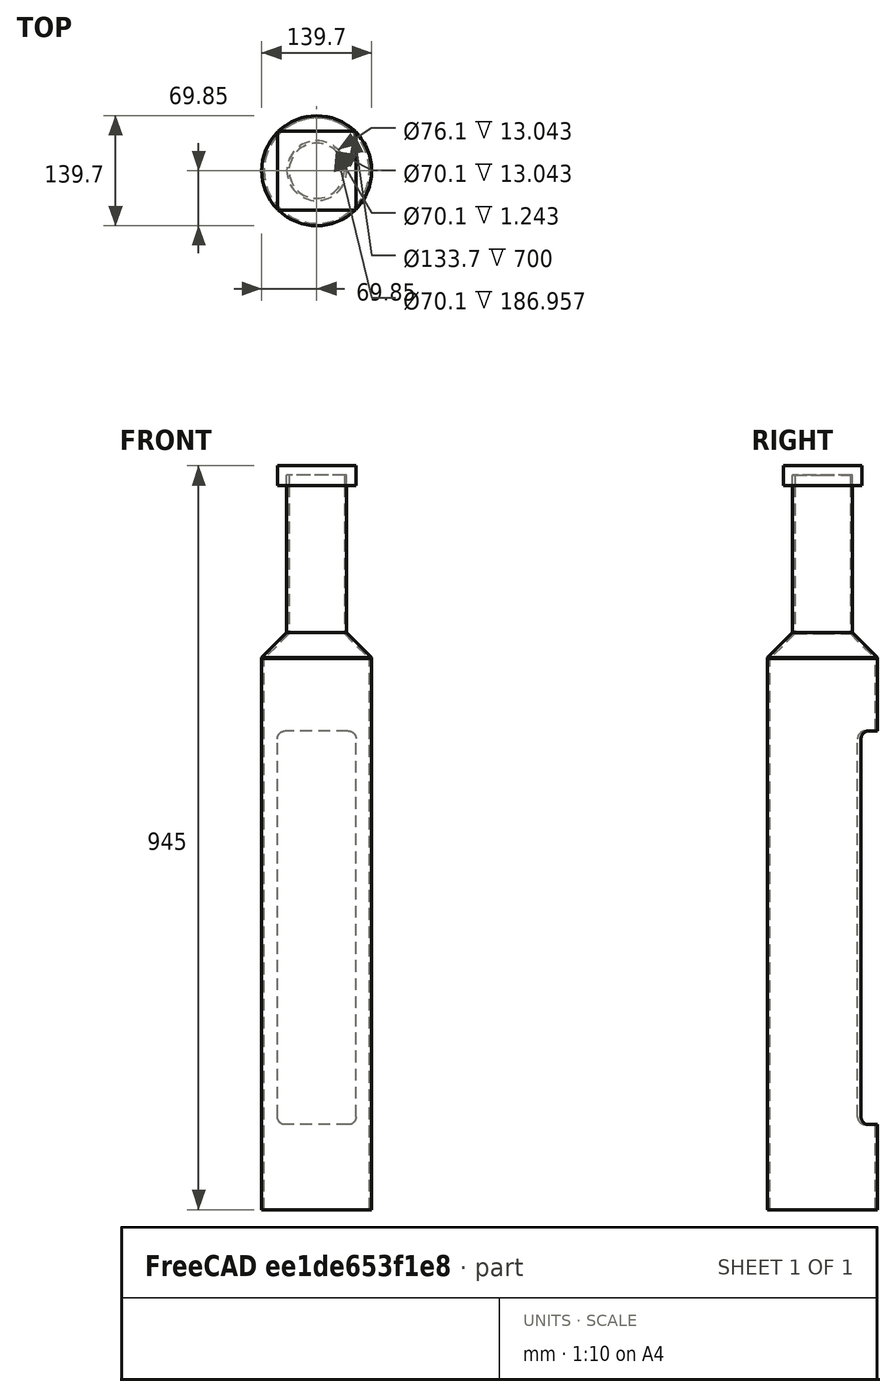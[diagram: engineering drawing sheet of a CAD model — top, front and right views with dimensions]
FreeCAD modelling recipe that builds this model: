
FCSTD DOCUMENT  (FreeCAD 0.21R33694 (Git))
Label: transition2
License: All rights reserved
LicenseURL: http://en.wikipedia.org/wiki/All_rights_reserved
objects: Sketcher::SketchObject×4, Fem::ConstraintForce×4, Part::Revolution×3, Part::FeaturePython×2, Part::Extrusion×1, Part::Cut×1, Part::Box×1, Fem::ConstraintFixed×1, Fem::FemMeshObjectPython×1, App::MaterialObjectPython×1, Fem::FemSolverObjectPython×1, Fem::FemAnalysis×1
note: 12 computed .brp shape members not serialized (recipe doc carries the construction recipe); baked Part::Feature solids carry a one-line shape summary decoded from their .brp

FEATURE [Sketcher::SketchObject] Sketch
  FullyConstrained = true
  Placement = pos=(0,0,0) rot=(1,0,0;1.5708rad)
  sketch-geometry (6):
    g0: LineSegment StartX=66.85 StartY=0 StartZ=0 EndX=69.85 EndY=0 EndZ=0
    g1: LineSegment StartX=35.05 StartY=33.0426 StartZ=0 EndX=38.05 EndY=33.0426 EndZ=0
    g2: LineSegment StartX=35.05 StartY=33.0426 StartZ=0 EndX=35.05 EndY=31.8 EndZ=0
    g3: LineSegment StartX=69.85 StartY=0 StartZ=0 EndX=69.85 EndY=1.24264 EndZ=0
    g4: LineSegment StartX=35.05 StartY=31.8 StartZ=0 EndX=66.85 EndY=0 EndZ=0
    g5: LineSegment StartX=38.05 StartY=33.0426 StartZ=0 EndX=69.85 EndY=1.24264 EndZ=0
  constraints (18):
    c: PointOnObject(g0,g-1)
    c: DistanceX(g-1,g1) = 35.05
    c: DistanceX(g-1,g0) = 66.85
    c: DistanceX(g0,g0) = 3
    c: Horizontal(g0)
    c: Horizontal(g1)
    c: DistanceX(g1,g1) = 3
    c: Coincident(g2,g1)
    c: Vertical(g2)
    c: Coincident(g3,g0)
    c: Vertical(g3)
    c: Coincident(g4,g2)
    c: Coincident(g4,g0)
    c: Coincident(g5,g1)
    c: Coincident(g5,g3)
    c: Angle(g4,g-1) = 0.785398
    c: DistanceY(g2,g2) = 1.24264
    c: DistanceY(g3,g3) = 1.24264
FEATURE [Sketcher::SketchObject] Sketch001
  ExternalGeometry = -> [Sketch]
  FullyConstrained = true
  Placement = pos=(0,0,0) rot=(1,0,0;1.5708rad)
  sketch-geometry (4):
    g0: LineSegment StartX=35.05 StartY=33.0426 StartZ=0 EndX=38.05 EndY=33.0426 EndZ=0
    g1: LineSegment StartX=38.05 StartY=33.0426 StartZ=0 EndX=38.05 EndY=233.043 EndZ=0
    g2: LineSegment StartX=38.05 StartY=233.043 StartZ=0 EndX=35.05 EndY=233.043 EndZ=0
    g3: LineSegment StartX=35.05 StartY=233.043 StartZ=0 EndX=35.05 EndY=33.0426 EndZ=0
  constraints (11):
    c: Coincident(g0,g1)
    c: Coincident(g1,g2)
    c: Coincident(g2,g3)
    c: Coincident(g3,g0)
    c: Horizontal(g0)
    c: Horizontal(g2)
    c: Vertical(g1)
    c: Vertical(g3)
    c: Coincident(g0,g-3)
    c: DistanceY(g1,g1) = 200
    c: DistanceX(g0,g0) = 3
FEATURE [Sketcher::SketchObject] Sketch002
  ExternalGeometry = -> [Sketch]
  FullyConstrained = true
  Placement = pos=(0,0,0) rot=(1,0,0;1.5708rad)
  sketch-geometry (4):
    g0: LineSegment StartX=66.85 StartY=0 StartZ=0 EndX=69.85 EndY=0 EndZ=0
    g1: LineSegment StartX=69.85 StartY=0 StartZ=0 EndX=69.85 EndY=-700 EndZ=0
    g2: LineSegment StartX=69.85 StartY=-700 StartZ=0 EndX=66.85 EndY=-700 EndZ=0
    g3: LineSegment StartX=66.85 StartY=-700 StartZ=0 EndX=66.85 EndY=0 EndZ=0
  constraints (11):
    c: Coincident(g0,g1)
    c: Coincident(g1,g2)
    c: Coincident(g2,g3)
    c: Coincident(g3,g0)
    c: Horizontal(g0)
    c: Horizontal(g2)
    c: Vertical(g1)
    c: Vertical(g3)
    c: Coincident(g0,g-3)
    c: DistanceX(g0,g0) = 3
    c: DistanceY(g1,g1) = 700
FEATURE [Part::Revolution] Revolve
  Angle = 360
  Axis = (0,0,1)
  Base = (0,0,0)
  FaceMakerClass = Part::FaceMakerBullseye
  Solid = true
  Source = -> Sketch
  Symmetric = false
FEATURE [Part::Revolution] Revolve001
  Angle = 360
  Axis = (0,0,1)
  Base = (0,0,0)
  FaceMakerClass = Part::FaceMakerBullseye
  Solid = true
  Source = -> Sketch001
  Symmetric = false
FEATURE [Part::Revolution] Revolve002
  Angle = 360
  Axis = (0,0,1)
  Base = (0,0,0)
  FaceMakerClass = Part::FaceMakerBullseye
  Solid = true
  Source = -> Sketch002
  Symmetric = false
FEATURE [Part::FeaturePython] BooleanFragments  # WARN: FeaturePython — macro-defined, semantics opaque (R4)
  Mode = 2
  Objects = -> [Revolve,Revolve001,Revolve002]
  Tolerance = 0
FEATURE [Sketcher::SketchObject] Sketch003
  ExternalGeometry = -> [Sketch]
  FullyConstrained = true
  Placement = pos=(0,70,0) rot=(0,0.707107,0.707107;3.14159rad)
  sketch-geometry (8):
    g0: LineSegment StartX=-40 StartY=-91.9574 StartZ=0 EndX=40 EndY=-91.9574 EndZ=0
    g1: LineSegment StartX=50 StartY=-101.957 StartZ=0 EndX=50 EndY=-581.957 EndZ=0
    g2: LineSegment StartX=40 StartY=-591.957 StartZ=0 EndX=-40 EndY=-591.957 EndZ=0
    g3: LineSegment StartX=-50 StartY=-581.957 StartZ=0 EndX=-50 EndY=-101.957 EndZ=0
    g4: ArcOfCircle CenterX=-40 CenterY=-101.957 CenterZ=0 NormalX=0 NormalY=0 NormalZ=1 AngleXU=0 Radius=10 StartAngle=1.5708 EndAngle=3.14159
    g5: ArcOfCircle CenterX=40 CenterY=-101.957 CenterZ=0 NormalX=0 NormalY=0 NormalZ=1 AngleXU=0 Radius=10 StartAngle=2e-16 EndAngle=1.5708
    g6: ArcOfCircle CenterX=-40 CenterY=-581.957 CenterZ=0 NormalX=0 NormalY=0 NormalZ=1 AngleXU=0 Radius=10 StartAngle=3.14159 EndAngle=4.71239
    g7: ArcOfCircle CenterX=40 CenterY=-581.957 CenterZ=0 NormalX=0 NormalY=0 NormalZ=1 AngleXU=0 Radius=10 StartAngle=4.71239 EndAngle=6.28319
  constraints (20):
    c: Horizontal(g0)
    c: Horizontal(g2)
    c: Vertical(g1)
    c: Vertical(g3)
    c: Tangent(g3,g4) = 1.5708
    c: Tangent(g0,g4) = 1.5708
    c: Tangent(g0,g5) = 1.5708
    c: Tangent(g1,g5) = 1.5708
    c: Tangent(g3,g6) = 1.5708
    c: Tangent(g2,g6) = 1.5708
    c: Tangent(g2,g7) = 1.5708
    c: Tangent(g1,g7) = 1.5708
    c: Radius(g4) = 10
    c: Radius(g5) = 10
    c: Radius(g6) = 10
    c: Radius(g7) = 10
    c: DistanceX(g3,g1) = 100
    c: DistanceY(g2,g0) = 500
    c: DistanceY(g0,g-3) = 125
    c: DistanceX(g-1,g1) = 50
FEATURE [Part::Extrusion] Extrude
  Base = -> Sketch003
  Dir = (0,1,0)
  DirMode = 2
  FaceMakerClass = Part::FaceMakerBullseye
  LengthFwd = 0
  LengthRev = 50
  Solid = true
  Symmetric = false
FEATURE [Part::Cut] Cut
  Base = -> BooleanFragments
  Tool = -> Extrude
FEATURE [Part::Box] Box  label="Cube"
  AttacherType = Attacher::AttachEngine3D
  Height = 25
  Length = 100
  Placement = pos=(-50,-50,220) rot=(0,0,1;0rad)
  Width = 100
FEATURE [Part::FeaturePython] BooleanFragments001  # WARN: FeaturePython — macro-defined, semantics opaque (R4)
  Mode = 2
  Objects = -> [Cut,Box]
  Tolerance = 0
FEATURE [Fem::ConstraintFixed] ConstraintFixed
  NormalDirection = (0,0,-1)
  References = -> [BooleanFragments001]
  Scale = 12
FEATURE [Fem::ConstraintForce] ConstraintForce  label="my_a"
  Direction = -> BooleanFragments001 [Edge3]
  DirectionVector = (0,0,-1)
  Force = 0.01
  NormalDirection = (-1,0,0)
  Points = (16) [(-50,50,220),(-50,50,228.333),(-50,50,236.667),(-50,50,245),(-50,16.6667,220),(-50,16.6667,228.333),(-50,16.6667,236.667),(-50,16.6667,245),+8 more]
  References = -> [BooleanFragments001]
  Reversed = true
FEATURE [Fem::ConstraintForce] ConstraintForce001  label="my_b"
  Direction = -> BooleanFragments001 [Edge11]
  DirectionVector = (0,0,1)
  Force = 0.01
  NormalDirection = (1,0,0)
  Points = (16) [(50,50,220),(50,50,228.333),(50,50,236.667),(50,50,245),(50,16.6667,220),(50,16.6667,228.333),(50,16.6667,236.667),(50,16.6667,245),(50,-16.6667,220),+7 more]
  References = -> [BooleanFragments001]
FEATURE [Fem::ConstraintForce] ConstraintForce002  label="mx_a"
  Direction = -> BooleanFragments001 [Edge11]
  DirectionVector = (0,0,-1)
  Force = 1000
  NormalDirection = (0,1,0)
  Points = (16) [(-50,50,220),(-50,50,228.333),(-50,50,236.667),(-50,50,245),(-16.6667,50,220),(-16.6667,50,228.333),(-16.6667,50,236.667),(-16.6667,50,245),+8 more]
  References = -> [BooleanFragments001]
  Reversed = true
FEATURE [Fem::ConstraintForce] ConstraintForce003  label="mx_b"
  Direction = -> BooleanFragments001 [Edge6]
  DirectionVector = (0,0,1)
  Force = 1000
  NormalDirection = (0,-1,0)
  Points = (16) [(-50,-50,220),(-50,-50,228.333),(-50,-50,236.667),(-50,-50,245),(-16.6667,-50,220),(-16.6667,-50,228.333),(-16.6667,-50,236.667),(-16.6667,-50,245),+8 more]
  References = -> [BooleanFragments001]
FEATURE [Fem::FemMeshObjectPython] FEMMeshGmsh001  label="FEMMeshGmsh"  # FEM object (typed FeaturePython)
  Algorithm2D = 0
  Algorithm3D = 0
  CharacteristicLengthMax = 10
  CharacteristicLengthMin = 0
  CoherenceMesh = true
  ElementDimension = 0
  ElementOrder = 1
  GeometryTolerance = 1e-06
  GroupsOfNodes = false
  HighOrderOptimize = 0
  MeshSizeFromCurvature = 12
  OptimizeNetgen = false
  OptimizeStd = true
  Part = -> BooleanFragments001
  RecombinationAlgorithm = 0
  Recombine3DAll = false
  RecombineAll = false
  SecondOrderLinear = false
FEATURE [App::MaterialObjectPython] MaterialSolid  # material (typed FeaturePython)
  Category = 0
  Material = AuthorAndLicense=(c) 2014 M. Münch - GNU Lesser General Public License (LGPL),CardName=Steel-St-E-315,Density=7800 kg/m^3,Father=Metal,+13 more (map truncated)
FEATURE [Fem::FemSolverObjectPython] SolverCcxTools  # FEM object (typed FeaturePython)
  AnalysisType = 0
  BeamShellResultOutput3D = false
  BucklingFactors = 1
  EigenmodeHighLimit = 1000000
  EigenmodeLowLimit = 0
  EigenmodesCount = 10
  GeometricalNonlinearity = 0
  IterationsControlParameterCutb = 0.25,0.5,0.75,0.85,,,1.5,
  IterationsControlParameterIter = 4,8,9,200,10,400,,200,,
  IterationsControlParameterTimeUse = false
  IterationsThermoMechMaximum = 2000
  IterationsUserDefinedIncrementations = false
  IterationsUserDefinedTimeStepLength = false
  MaterialNonlinearity = 0
  MatrixSolverType = 0
  SplitInputWriter = false
  ThermoMechSteadyState = true
  TimeEnd = 1
  TimeInitialStep = 0.01
FEATURE [Fem::FemAnalysis] Analysis
  Group = -> [ConstraintFixed,ConstraintForce,ConstraintForce001,ConstraintForce002,ConstraintForce003,FEMMeshGmsh001,MaterialSolid,SolverCcxTools]
